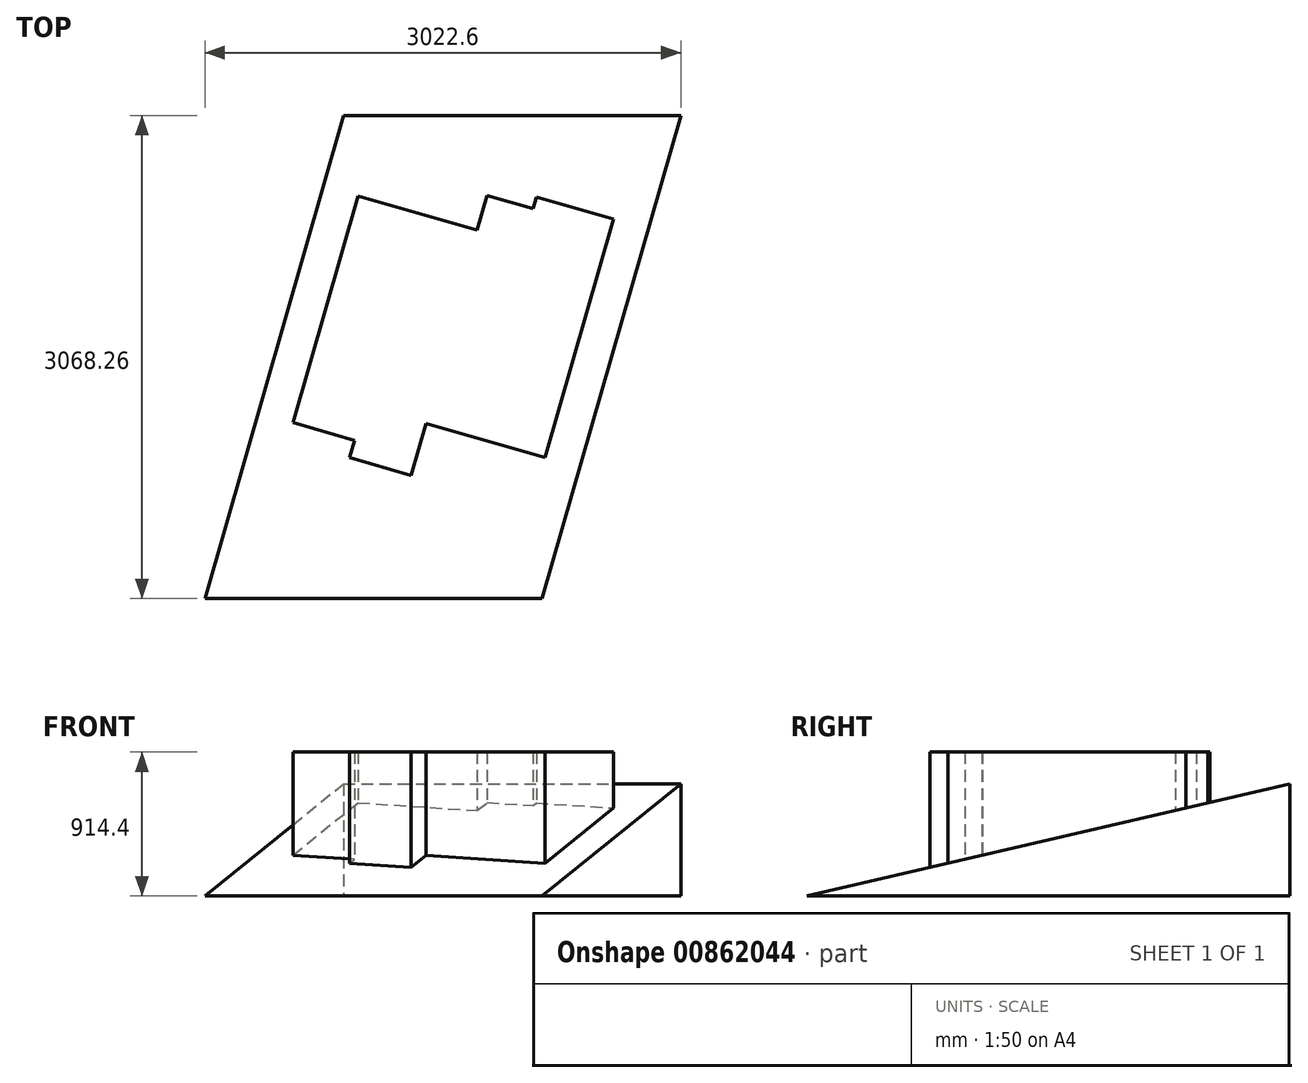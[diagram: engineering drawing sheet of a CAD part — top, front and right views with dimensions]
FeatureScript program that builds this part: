
annotation { "Feature Type Name" : "Feature", "Feature Type Description" : "" }
export const myFeature = defineFeature(function(context is Context, id is Id, definition is map)
    precondition{}
    {
        {
            var Q0;
            Q0=qCreatedBy(makeId("Right.planeOp"),FACE);
            var sketch = newSketch(context, id + "F0", { "sketchPlane" : qUnion([Q0])});
            skLineSegment(sketch, "E0", {"start": v(0, 0) * mm, "end": v(-1534.13, -355.6) * mm});
            skLineSegment(sketch, "E1", {"start": v(0, 0) * mm, "end": v(1534.13, 355.6) * mm});
            skLineSegment(sketch, "E2", {"start": v(-1534.13, -355.6) * mm, "end": v(1534.13, -355.6) * mm});
            skLineSegment(sketch, "E3", {"start": v(1534.13, -355.6) * mm, "end": v(1534.13, 355.6) * mm});
            skSolve(sketch);
        }
        {
            var Q0;
            Q0=makeQuery(id+"F0.imprint","IMPRINT",FACE,{"disambiguationData":[TD([[makeQuery(id+"F0.imprint","IMPRINT",EDGE,{"derivedFrom":sQuery(id+"F0.wireOp",EDGE,"E0")}),1.0]])]});
            extrude(context, id + "F1", {"entities" : qUnion([Q0]), "endBound" : BoundingType.SYMMETRIC, "oppositeDirection" : true, "depth" : 3022.6 * mm, "offsetDistance" : 25.4 * mm});
        }
        {
            var Q0;
            Q0=makeQuery(id+"F1.opExtrude","SWEPT_FACE",FACE,{"disambiguationData":[OSD([sQuery(id+"F0.wireOp",EDGE,"E2")])]});
            var sketch = newSketch(context, id + "F2", { "sketchPlane" : qUnion([Q0])});
            skLineSegment(sketch, "E4", {"start": v(1511.3, -1534.13) * mm, "end": v(631.5, 1534.13) * mm});
            skLineSegment(sketch, "E5", {"start": v(-1511.3, 1534.13) * mm, "end": v(-631.5, -1534.13) * mm});
            skLineSegment(sketch, "E6", {"start": v(-1511.3, 1534.13) * mm, "end": v(-1511.3, -1534.13) * mm});
            skLineSegment(sketch, "E7", {"start": v(-1511.3, -1534.13) * mm, "end": v(-631.5, -1534.13) * mm});
            skLineSegment(sketch, "E8", {"start": v(1511.3, -1534.13) * mm, "end": v(1511.3, 1534.13) * mm});
            skLineSegment(sketch, "E9", {"start": v(1511.3, 1534.13) * mm, "end": v(631.5, 1534.13) * mm});
            skSolve(sketch);
        }
        {
            var Q0;
            Q0 = qSketchRegion(id + "F2", true);
            extrude(context, id + "F3", {"entities" : qUnion([Q0]), "operationType" : NewBodyOperationType.REMOVE, "endBound" : BoundingType.THROUGH_ALL, "oppositeDirection" : true, "depth" : 25.4 * mm, "offsetDistance" : 25.4 * mm});
        }
        {
            var Q0;
            Q0=makeQuery(id+"F1.opExtrude","SWEPT_FACE",FACE,{"disambiguationData":[OSD([sQuery(id+"F0.wireOp",EDGE,"E2")])]});
            var sketch = newSketch(context, id + "F4", { "sketchPlane" : qUnion([Q0])});
            skLineSegment(sketch, "E10", {"start": v(-538.88, -1023.42) * mm, "end": v(218.01, -806.38) * mm});
            skLineSegment(sketch, "E11", {"start": v(218.01, -806.38) * mm, "end": v(281.03, -1026.13) * mm});
            skLineSegment(sketch, "E12", {"start": v(281.03, -1026.13) * mm, "end": v(574.02, -942.11) * mm});
            skLineSegment(sketch, "E13", {"start": v(574.02, -942.11) * mm, "end": v(595.02, -1015.36) * mm});
            skLineSegment(sketch, "E14", {"start": v(595.02, -1015.36) * mm, "end": v(1083.34, -875.34) * mm});
            skLineSegment(sketch, "E15", {"start": v(-538.88, -1023.42) * mm, "end": v(-759.77, -1086.76) * mm, "construction": true});
            skLineSegment(sketch, "E16", {"start": v(1083.34, -875.34) * mm, "end": v(1304.23, -812) * mm, "construction": true});
            skLineSegment(sketch, "E17", {"start": v(281.03, -1534.13) * mm, "end": v(281.03, -1026.13) * mm, "construction": true});
            skLineSegment(sketch, "E18", {"start": v(1083.34, -875.34) * mm, "end": v(649.27, 638.46) * mm});
            skLineSegment(sketch, "E19", {"start": v(649.27, 638.46) * mm, "end": v(-107.63, 421.42) * mm});
            skLineSegment(sketch, "E20", {"start": v(-107.63, 421.42) * mm, "end": v(-202.14, 751.04) * mm});
            skLineSegment(sketch, "E21", {"start": v(-202.14, 751.04) * mm, "end": v(-592.8, 639.02) * mm});
            skLineSegment(sketch, "E22", {"start": v(-592.8, 639.02) * mm, "end": v(-561.3, 529.15) * mm});
            skLineSegment(sketch, "E23", {"start": v(-561.3, 529.15) * mm, "end": v(-951.95, 417.13) * mm});
            skLineSegment(sketch, "E24", {"start": v(-951.95, 417.13) * mm, "end": v(-538.88, -1023.42) * mm});
            skSolve(sketch);
        }
        {
            var Q0;
            Q0 = qSketchRegion(id + "F4", true);
            extrude(context, id + "F5", {"entities" : qUnion([Q0]), "operationType" : NewBodyOperationType.ADD, "oppositeDirection" : true, "depth" : 914.4 * mm, "offsetDistance" : 25.4 * mm});
        }
    });
